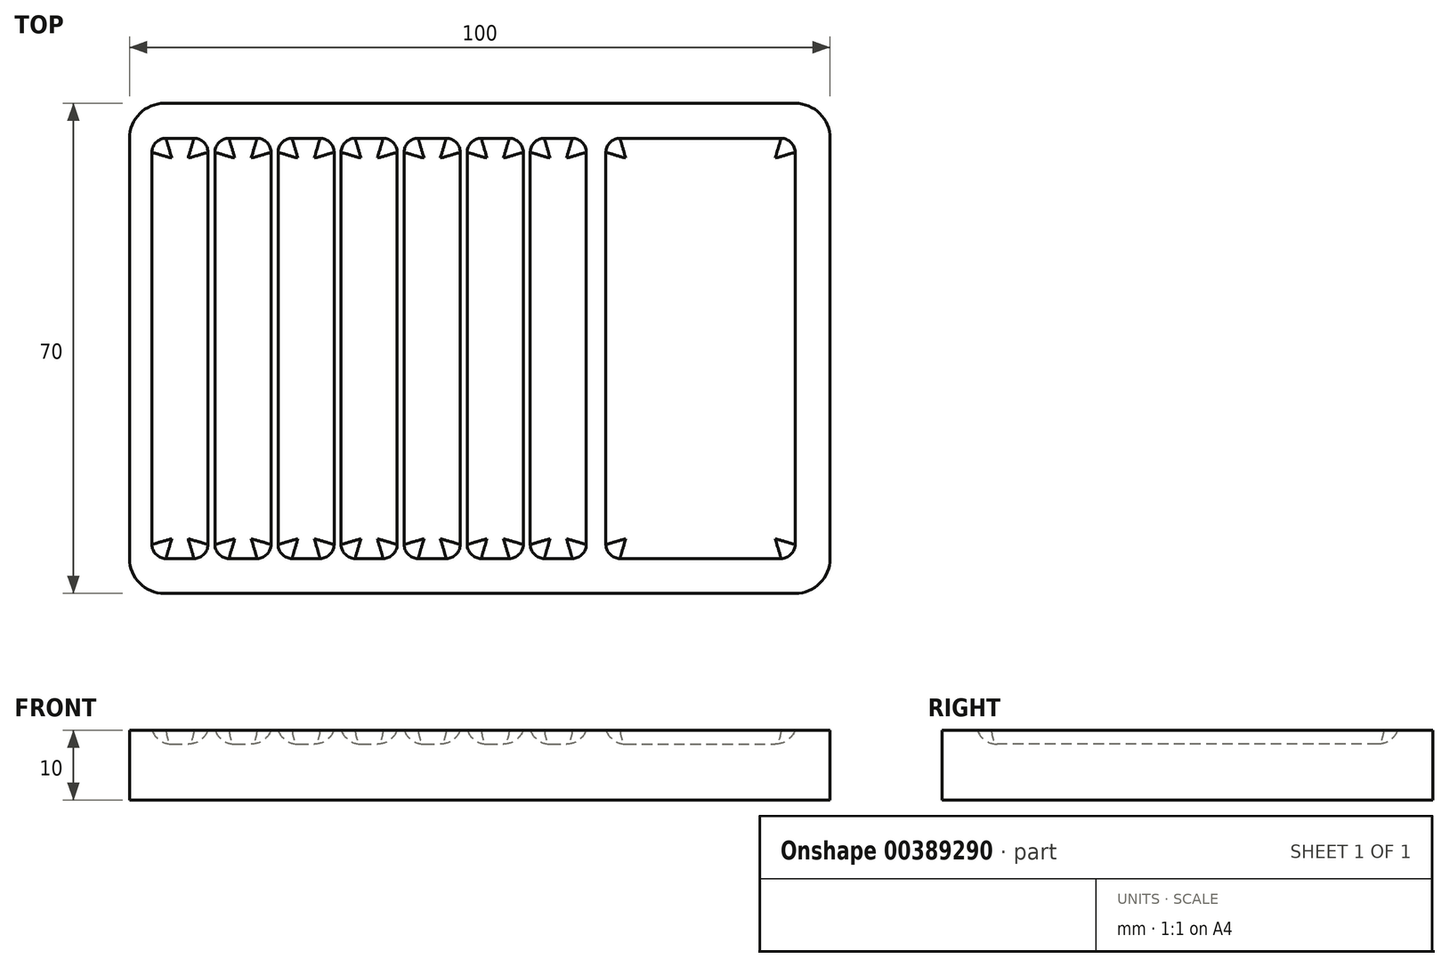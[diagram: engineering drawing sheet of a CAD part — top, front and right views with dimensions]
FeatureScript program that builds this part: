
annotation { "Feature Type Name" : "Feature", "Feature Type Description" : "" }
export const myFeature = defineFeature(function(context is Context, id is Id, definition is map)
    precondition{}
    {
        {
            var Q0;
            Q0=qCreatedBy(makeId("Top.planeOp"),FACE);
            var sketch = newSketch(context, id + "F0", { "sketchPlane" : qUnion([Q0])});
            skLineSegment(sketch, "E0.bottom", {"start": v(0, 0) * mm, "end": v(-100, 0) * mm});
            skLineSegment(sketch, "E0.top", {"start": v(0, 70) * mm, "end": v(-100, 70) * mm});
            skLineSegment(sketch, "E0.left", {"start": v(0, 0) * mm, "end": v(0, 70) * mm});
            skLineSegment(sketch, "E0.right", {"start": v(-100, 0) * mm, "end": v(-100, 70) * mm});
            skSolve(sketch);
        }
        {
            var Q0;
            Q0 = qSketchRegion(id + "F0", true);
            extrude(context, id + "F1", {"entities" : qUnion([Q0]), "depth" : 10 * mm, "offsetDistance" : 25 * mm});
        }
        {
            var Q0;
            Q0=makeQuery(id+"F1.opExtrude","CAP_FACE",FACE,{"disambiguationData":[OSD([sQuery(id+"F0.wireOp",EDGE,"E0.bottom"),sQuery(id+"F0.wireOp",EDGE,"E0.top"),sQuery(id+"F0.wireOp",EDGE,"E0.left"),sQuery(id+"F0.wireOp",EDGE,"E0.right")])],"isStart":false});
            var sketch = newSketch(context, id + "F2", { "sketchPlane" : qUnion([Q0])});
            skLineSegment(sketch, "E1.bottom", {"start": v(-94.8, 65) * mm, "end": v(-90.8, 65) * mm});
            skLineSegment(sketch, "E1.top", {"start": v(-94.8, 5) * mm, "end": v(-90.8, 5) * mm});
            skLineSegment(sketch, "E1.left", {"start": v(-96.8, 63) * mm, "end": v(-96.8, 7) * mm});
            skLineSegment(sketch, "E1.right", {"start": v(-88.8, 63) * mm, "end": v(-88.8, 7) * mm});
            skPoint(sketch, "E2.visualSharp", {"position": v(-88.8, 65) * mm});
            skArc(sketch, "E2.filletArc", {"start": v(-88.8, 63) * mm, "mid": v(-89.38, 64.41) * mm, "end": v(-90.8, 65) * mm});
            skPoint(sketch, "E3.visualSharp", {"position": v(-96.8, 65) * mm});
            skArc(sketch, "E3.filletArc", {"start": v(-94.8, 65) * mm, "mid": v(-96.2, 64.41) * mm, "end": v(-96.8, 63) * mm});
            skPoint(sketch, "E4.visualSharp", {"position": v(-88.8, 5) * mm});
            skArc(sketch, "E4.filletArc", {"start": v(-90.8, 5) * mm, "mid": v(-89.38, 5.59) * mm, "end": v(-88.8, 7) * mm});
            skPoint(sketch, "E5.visualSharp", {"position": v(-96.8, 5) * mm});
            skArc(sketch, "E5.filletArc", {"start": v(-96.8, 7) * mm, "mid": v(-96.2, 5.59) * mm, "end": v(-94.8, 5) * mm});
            skLineSegment(sketch, "E6.1.0.0", {"start": v(-79.8, 63) * mm, "end": v(-79.8, 7) * mm});
            skPoint(sketch, "E6.1.0.1", {"position": v(-79.8, 65) * mm});
            skLineSegment(sketch, "E6.1.0.2", {"start": v(-87.8, 63) * mm, "end": v(-87.8, 7) * mm});
            skPoint(sketch, "E6.1.0.3", {"position": v(-87.8, 65) * mm});
            skPoint(sketch, "E6.1.0.4", {"position": v(-87.8, 5) * mm});
            skPoint(sketch, "E6.1.0.5", {"position": v(-79.8, 5) * mm});
            skArc(sketch, "E6.1.0.6", {"start": v(-79.8, 63) * mm, "mid": v(-80.38, 64.41) * mm, "end": v(-81.8, 65) * mm});
            skArc(sketch, "E6.1.0.7", {"start": v(-81.8, 5) * mm, "mid": v(-80.38, 5.59) * mm, "end": v(-79.8, 7) * mm});
            skArc(sketch, "E6.1.0.8", {"start": v(-87.8, 7) * mm, "mid": v(-87.2, 5.59) * mm, "end": v(-85.8, 5) * mm});
            skArc(sketch, "E6.1.0.9", {"start": v(-85.8, 65) * mm, "mid": v(-87.2, 64.41) * mm, "end": v(-87.8, 63) * mm});
            skLineSegment(sketch, "E6.1.0.10", {"start": v(-85.8, 5) * mm, "end": v(-81.8, 5) * mm});
            skLineSegment(sketch, "E6.1.0.11", {"start": v(-85.8, 65) * mm, "end": v(-81.8, 65) * mm});
            skLineSegment(sketch, "E6.2.0.0", {"start": v(-70.8, 63) * mm, "end": v(-70.8, 7) * mm});
            skPoint(sketch, "E6.2.0.1", {"position": v(-70.8, 65) * mm});
            skLineSegment(sketch, "E6.2.0.2", {"start": v(-78.8, 63) * mm, "end": v(-78.8, 7) * mm});
            skPoint(sketch, "E6.2.0.3", {"position": v(-78.8, 65) * mm});
            skPoint(sketch, "E6.2.0.4", {"position": v(-78.8, 5) * mm});
            skPoint(sketch, "E6.2.0.5", {"position": v(-70.8, 5) * mm});
            skArc(sketch, "E6.2.0.6", {"start": v(-70.8, 63) * mm, "mid": v(-71.38, 64.41) * mm, "end": v(-72.8, 65) * mm});
            skArc(sketch, "E6.2.0.7", {"start": v(-72.8, 5) * mm, "mid": v(-71.38, 5.59) * mm, "end": v(-70.8, 7) * mm});
            skArc(sketch, "E6.2.0.8", {"start": v(-78.8, 7) * mm, "mid": v(-78.2, 5.59) * mm, "end": v(-76.8, 5) * mm});
            skArc(sketch, "E6.2.0.9", {"start": v(-76.8, 65) * mm, "mid": v(-78.2, 64.41) * mm, "end": v(-78.8, 63) * mm});
            skLineSegment(sketch, "E6.2.0.10", {"start": v(-76.8, 5) * mm, "end": v(-72.8, 5) * mm});
            skLineSegment(sketch, "E6.2.0.11", {"start": v(-76.8, 65) * mm, "end": v(-72.8, 65) * mm});
            skLineSegment(sketch, "E6.3.0.0", {"start": v(-61.8, 63) * mm, "end": v(-61.8, 7) * mm});
            skPoint(sketch, "E6.3.0.1", {"position": v(-61.8, 65) * mm});
            skLineSegment(sketch, "E6.3.0.2", {"start": v(-69.8, 63) * mm, "end": v(-69.8, 7) * mm});
            skPoint(sketch, "E6.3.0.3", {"position": v(-69.8, 65) * mm});
            skPoint(sketch, "E6.3.0.4", {"position": v(-69.8, 5) * mm});
            skPoint(sketch, "E6.3.0.5", {"position": v(-61.8, 5) * mm});
            skArc(sketch, "E6.3.0.6", {"start": v(-61.8, 63) * mm, "mid": v(-62.38, 64.41) * mm, "end": v(-63.8, 65) * mm});
            skArc(sketch, "E6.3.0.7", {"start": v(-63.8, 5) * mm, "mid": v(-62.38, 5.59) * mm, "end": v(-61.8, 7) * mm});
            skArc(sketch, "E6.3.0.8", {"start": v(-69.8, 7) * mm, "mid": v(-69.2, 5.59) * mm, "end": v(-67.8, 5) * mm});
            skArc(sketch, "E6.3.0.9", {"start": v(-67.8, 65) * mm, "mid": v(-69.2, 64.41) * mm, "end": v(-69.8, 63) * mm});
            skLineSegment(sketch, "E6.3.0.10", {"start": v(-67.8, 5) * mm, "end": v(-63.8, 5) * mm});
            skLineSegment(sketch, "E6.3.0.11", {"start": v(-67.8, 65) * mm, "end": v(-63.8, 65) * mm});
            skLineSegment(sketch, "E6.4.0.0", {"start": v(-52.8, 63) * mm, "end": v(-52.8, 7) * mm});
            skPoint(sketch, "E6.4.0.1", {"position": v(-52.8, 65) * mm});
            skLineSegment(sketch, "E6.4.0.2", {"start": v(-60.8, 63) * mm, "end": v(-60.8, 7) * mm});
            skPoint(sketch, "E6.4.0.3", {"position": v(-60.8, 65) * mm});
            skPoint(sketch, "E6.4.0.4", {"position": v(-60.8, 5) * mm});
            skPoint(sketch, "E6.4.0.5", {"position": v(-52.8, 5) * mm});
            skArc(sketch, "E6.4.0.6", {"start": v(-52.8, 63) * mm, "mid": v(-53.38, 64.41) * mm, "end": v(-54.8, 65) * mm});
            skArc(sketch, "E6.4.0.7", {"start": v(-54.8, 5) * mm, "mid": v(-53.38, 5.59) * mm, "end": v(-52.8, 7) * mm});
            skArc(sketch, "E6.4.0.8", {"start": v(-60.8, 7) * mm, "mid": v(-60.2, 5.59) * mm, "end": v(-58.8, 5) * mm});
            skArc(sketch, "E6.4.0.9", {"start": v(-58.8, 65) * mm, "mid": v(-60.2, 64.41) * mm, "end": v(-60.8, 63) * mm});
            skLineSegment(sketch, "E6.4.0.10", {"start": v(-58.8, 5) * mm, "end": v(-54.8, 5) * mm});
            skLineSegment(sketch, "E6.4.0.11", {"start": v(-58.8, 65) * mm, "end": v(-54.8, 65) * mm});
            skLineSegment(sketch, "E6.5.0.0", {"start": v(-43.8, 63) * mm, "end": v(-43.8, 7) * mm});
            skPoint(sketch, "E6.5.0.1", {"position": v(-43.8, 65) * mm});
            skLineSegment(sketch, "E6.5.0.2", {"start": v(-51.8, 63) * mm, "end": v(-51.8, 7) * mm});
            skPoint(sketch, "E6.5.0.3", {"position": v(-51.8, 65) * mm});
            skPoint(sketch, "E6.5.0.4", {"position": v(-51.8, 5) * mm});
            skPoint(sketch, "E6.5.0.5", {"position": v(-43.8, 5) * mm});
            skArc(sketch, "E6.5.0.6", {"start": v(-43.8, 63) * mm, "mid": v(-44.38, 64.41) * mm, "end": v(-45.8, 65) * mm});
            skArc(sketch, "E6.5.0.7", {"start": v(-45.8, 5) * mm, "mid": v(-44.38, 5.59) * mm, "end": v(-43.8, 7) * mm});
            skArc(sketch, "E6.5.0.8", {"start": v(-51.8, 7) * mm, "mid": v(-51.2, 5.59) * mm, "end": v(-49.8, 5) * mm});
            skArc(sketch, "E6.5.0.9", {"start": v(-49.8, 65) * mm, "mid": v(-51.2, 64.41) * mm, "end": v(-51.8, 63) * mm});
            skLineSegment(sketch, "E6.5.0.10", {"start": v(-49.8, 5) * mm, "end": v(-45.8, 5) * mm});
            skLineSegment(sketch, "E6.5.0.11", {"start": v(-49.8, 65) * mm, "end": v(-45.8, 65) * mm});
            skLineSegment(sketch, "E6.6.0.0", {"start": v(-34.8, 63) * mm, "end": v(-34.8, 7) * mm});
            skPoint(sketch, "E6.6.0.1", {"position": v(-34.8, 65) * mm});
            skLineSegment(sketch, "E6.6.0.2", {"start": v(-42.8, 63) * mm, "end": v(-42.8, 7) * mm});
            skPoint(sketch, "E6.6.0.3", {"position": v(-42.8, 65) * mm});
            skPoint(sketch, "E6.6.0.4", {"position": v(-42.8, 5) * mm});
            skPoint(sketch, "E6.6.0.5", {"position": v(-34.8, 5) * mm});
            skArc(sketch, "E6.6.0.6", {"start": v(-34.8, 63) * mm, "mid": v(-35.38, 64.41) * mm, "end": v(-36.8, 65) * mm});
            skArc(sketch, "E6.6.0.7", {"start": v(-36.8, 5) * mm, "mid": v(-35.38, 5.59) * mm, "end": v(-34.8, 7) * mm});
            skArc(sketch, "E6.6.0.8", {"start": v(-42.8, 7) * mm, "mid": v(-42.2, 5.59) * mm, "end": v(-40.8, 5) * mm});
            skArc(sketch, "E6.6.0.9", {"start": v(-40.8, 65) * mm, "mid": v(-42.2, 64.41) * mm, "end": v(-42.8, 63) * mm});
            skLineSegment(sketch, "E6.6.0.10", {"start": v(-40.8, 5) * mm, "end": v(-36.8, 5) * mm});
            skLineSegment(sketch, "E6.6.0.11", {"start": v(-40.8, 65) * mm, "end": v(-36.8, 65) * mm});
            skLineSegment(sketch, "E6.direction1", {"start": v(-96.8, 5) * mm, "end": v(-87.8, 5) * mm, "construction": true});
            skLineSegment(sketch, "E7.bottom", {"start": v(-30, 65) * mm, "end": v(-7, 65) * mm});
            skLineSegment(sketch, "E7.top", {"start": v(-30, 5) * mm, "end": v(-7, 5) * mm});
            skLineSegment(sketch, "E7.left", {"start": v(-32, 63) * mm, "end": v(-32, 7) * mm});
            skLineSegment(sketch, "E7.right", {"start": v(-5, 63) * mm, "end": v(-5, 7) * mm});
            skPoint(sketch, "E8.visualSharp", {"position": v(-32, 65) * mm});
            skArc(sketch, "E8.filletArc", {"start": v(-30, 65) * mm, "mid": v(-31.41, 64.41) * mm, "end": v(-32, 63) * mm});
            skPoint(sketch, "E9.visualSharp", {"position": v(-5, 65) * mm});
            skArc(sketch, "E9.filletArc", {"start": v(-5, 63) * mm, "mid": v(-5.59, 64.41) * mm, "end": v(-7, 65) * mm});
            skPoint(sketch, "E10.visualSharp", {"position": v(-5, 5) * mm});
            skArc(sketch, "E10.filletArc", {"start": v(-7, 5) * mm, "mid": v(-5.59, 5.59) * mm, "end": v(-5, 7) * mm});
            skPoint(sketch, "E11.visualSharp", {"position": v(-32, 5) * mm});
            skArc(sketch, "E11.filletArc", {"start": v(-32, 7) * mm, "mid": v(-31.41, 5.59) * mm, "end": v(-30, 5) * mm});
            skSolve(sketch);
        }
        {
            var Q0;
            Q0=makeQuery(id+"F2.imprint","IMPRINT",FACE,{"disambiguationData":[TD([[makeQuery(id+"F2.imprint","IMPRINT",EDGE,{"derivedFrom":sQuery(id+"F2.wireOp",EDGE,"E6.1.0.0")}),-1.0]])]});
            var Q1;
            Q1=makeQuery(id+"F2.imprint","IMPRINT",FACE,{"disambiguationData":[TD([[makeQuery(id+"F2.imprint","IMPRINT",EDGE,{"derivedFrom":sQuery(id+"F2.wireOp",EDGE,"E6.2.0.0")}),-1.0]])]});
            var Q2;
            Q2=makeQuery(id+"F2.imprint","IMPRINT",FACE,{"disambiguationData":[TD([[makeQuery(id+"F2.imprint","IMPRINT",EDGE,{"derivedFrom":sQuery(id+"F2.wireOp",EDGE,"E6.3.0.0")}),-1.0]])]});
            var Q3;
            Q3=makeQuery(id+"F2.imprint","IMPRINT",FACE,{"disambiguationData":[TD([[makeQuery(id+"F2.imprint","IMPRINT",EDGE,{"derivedFrom":sQuery(id+"F2.wireOp",EDGE,"E6.4.0.0")}),-1.0]])]});
            var Q4;
            Q4=makeQuery(id+"F2.imprint","IMPRINT",FACE,{"disambiguationData":[TD([[makeQuery(id+"F2.imprint","IMPRINT",EDGE,{"derivedFrom":sQuery(id+"F2.wireOp",EDGE,"E6.5.0.0")}),-1.0]])]});
            var Q5;
            Q5=makeQuery(id+"F2.imprint","IMPRINT",FACE,{"disambiguationData":[TD([[makeQuery(id+"F2.imprint","IMPRINT",EDGE,{"derivedFrom":sQuery(id+"F2.wireOp",EDGE,"E6.6.0.0")}),-1.0]])]});
            var Q6;
            Q6=makeQuery(id+"F2.imprint","IMPRINT",FACE,{"disambiguationData":[TD([[makeQuery(id+"F2.imprint","IMPRINT",EDGE,{"derivedFrom":sQuery(id+"F2.wireOp",EDGE,"E1.bottom")}),-1.0]])]});
            var Q7;
            Q7=makeQuery(id+"F2.imprint","IMPRINT",FACE,{"disambiguationData":[TD([[makeQuery(id+"F2.imprint","IMPRINT",EDGE,{"derivedFrom":sQuery(id+"F2.wireOp",EDGE,"E7.bottom")}),-1.0]])]});
            extrude(context, id + "F3", {"entities" : qUnion([Q0, Q1, Q2, Q3, Q4, Q5, Q6, Q7]), "operationType" : NewBodyOperationType.REMOVE, "oppositeDirection" : true, "depth" : 2 * mm, "offsetDistance" : 25 * mm});
        }
        {
            var Q0;
            Q0=makeQuery(id+"F3.boolean.opBoolean","COPY",FACE,{"derivedFrom":makeQuery(id+"F3.opExtrude","CAP_FACE",FACE,{"disambiguationData":[OSD([sQuery(id+"F2.wireOp",EDGE,"E1.bottom"),sQuery(id+"F2.wireOp",EDGE,"E1.top"),sQuery(id+"F2.wireOp",EDGE,"E1.left"),sQuery(id+"F2.wireOp",EDGE,"E1.right"),sQuery(id+"F2.wireOp",EDGE,"E2.filletArc"),sQuery(id+"F2.wireOp",EDGE,"E3.filletArc"),sQuery(id+"F2.wireOp",EDGE,"E4.filletArc"),sQuery(id+"F2.wireOp",EDGE,"E5.filletArc")])],"isStart":false})});
            var Q1;
            Q1=makeQuery(id+"F3.boolean.opBoolean","COPY",FACE,{"derivedFrom":makeQuery(id+"F3.opExtrude","CAP_FACE",FACE,{"disambiguationData":[OSD([sQuery(id+"F2.wireOp",EDGE,"E7.bottom"),sQuery(id+"F2.wireOp",EDGE,"E7.top"),sQuery(id+"F2.wireOp",EDGE,"E7.left"),sQuery(id+"F2.wireOp",EDGE,"E7.right"),sQuery(id+"F2.wireOp",EDGE,"E8.filletArc"),sQuery(id+"F2.wireOp",EDGE,"E9.filletArc"),sQuery(id+"F2.wireOp",EDGE,"E10.filletArc"),sQuery(id+"F2.wireOp",EDGE,"E11.filletArc")])],"isStart":false})});
            var Q2;
            Q2=makeQuery(id+"F3.boolean.opBoolean","COPY",FACE,{"derivedFrom":makeQuery(id+"F3.opExtrude","CAP_FACE",FACE,{"disambiguationData":[OSD([sQuery(id+"F2.wireOp",EDGE,"E6.1.0.0"),sQuery(id+"F2.wireOp",EDGE,"E6.1.0.2"),sQuery(id+"F2.wireOp",EDGE,"E6.1.0.6"),sQuery(id+"F2.wireOp",EDGE,"E6.1.0.7"),sQuery(id+"F2.wireOp",EDGE,"E6.1.0.8"),sQuery(id+"F2.wireOp",EDGE,"E6.1.0.9"),sQuery(id+"F2.wireOp",EDGE,"E6.1.0.10"),sQuery(id+"F2.wireOp",EDGE,"E6.1.0.11")])],"isStart":false})});
            var Q3;
            Q3=makeQuery(id+"F3.boolean.opBoolean","COPY",FACE,{"derivedFrom":makeQuery(id+"F3.opExtrude","CAP_FACE",FACE,{"disambiguationData":[OSD([sQuery(id+"F2.wireOp",EDGE,"E6.2.0.0"),sQuery(id+"F2.wireOp",EDGE,"E6.2.0.2"),sQuery(id+"F2.wireOp",EDGE,"E6.2.0.6"),sQuery(id+"F2.wireOp",EDGE,"E6.2.0.7"),sQuery(id+"F2.wireOp",EDGE,"E6.2.0.8"),sQuery(id+"F2.wireOp",EDGE,"E6.2.0.9"),sQuery(id+"F2.wireOp",EDGE,"E6.2.0.10"),sQuery(id+"F2.wireOp",EDGE,"E6.2.0.11")])],"isStart":false})});
            var Q4;
            Q4=makeQuery(id+"F3.boolean.opBoolean","COPY",FACE,{"derivedFrom":makeQuery(id+"F3.opExtrude","CAP_FACE",FACE,{"disambiguationData":[OSD([sQuery(id+"F2.wireOp",EDGE,"E6.3.0.0"),sQuery(id+"F2.wireOp",EDGE,"E6.3.0.2"),sQuery(id+"F2.wireOp",EDGE,"E6.3.0.6"),sQuery(id+"F2.wireOp",EDGE,"E6.3.0.7"),sQuery(id+"F2.wireOp",EDGE,"E6.3.0.8"),sQuery(id+"F2.wireOp",EDGE,"E6.3.0.9"),sQuery(id+"F2.wireOp",EDGE,"E6.3.0.10"),sQuery(id+"F2.wireOp",EDGE,"E6.3.0.11")])],"isStart":false})});
            var Q5;
            Q5=makeQuery(id+"F3.boolean.opBoolean","COPY",FACE,{"derivedFrom":makeQuery(id+"F3.opExtrude","CAP_FACE",FACE,{"disambiguationData":[OSD([sQuery(id+"F2.wireOp",EDGE,"E6.4.0.0"),sQuery(id+"F2.wireOp",EDGE,"E6.4.0.2"),sQuery(id+"F2.wireOp",EDGE,"E6.4.0.6"),sQuery(id+"F2.wireOp",EDGE,"E6.4.0.7"),sQuery(id+"F2.wireOp",EDGE,"E6.4.0.8"),sQuery(id+"F2.wireOp",EDGE,"E6.4.0.9"),sQuery(id+"F2.wireOp",EDGE,"E6.4.0.10"),sQuery(id+"F2.wireOp",EDGE,"E6.4.0.11")])],"isStart":false})});
            var Q6;
            Q6=makeQuery(id+"F3.boolean.opBoolean","COPY",FACE,{"derivedFrom":makeQuery(id+"F3.opExtrude","CAP_FACE",FACE,{"disambiguationData":[OSD([sQuery(id+"F2.wireOp",EDGE,"E6.5.0.0"),sQuery(id+"F2.wireOp",EDGE,"E6.5.0.2"),sQuery(id+"F2.wireOp",EDGE,"E6.5.0.6"),sQuery(id+"F2.wireOp",EDGE,"E6.5.0.7"),sQuery(id+"F2.wireOp",EDGE,"E6.5.0.8"),sQuery(id+"F2.wireOp",EDGE,"E6.5.0.9"),sQuery(id+"F2.wireOp",EDGE,"E6.5.0.10"),sQuery(id+"F2.wireOp",EDGE,"E6.5.0.11")])],"isStart":false})});
            var Q7;
            Q7=makeQuery(id+"F3.boolean.opBoolean","COPY",FACE,{"derivedFrom":makeQuery(id+"F3.opExtrude","CAP_FACE",FACE,{"disambiguationData":[OSD([sQuery(id+"F2.wireOp",EDGE,"E6.6.0.0"),sQuery(id+"F2.wireOp",EDGE,"E6.6.0.2"),sQuery(id+"F2.wireOp",EDGE,"E6.6.0.6"),sQuery(id+"F2.wireOp",EDGE,"E6.6.0.7"),sQuery(id+"F2.wireOp",EDGE,"E6.6.0.8"),sQuery(id+"F2.wireOp",EDGE,"E6.6.0.9"),sQuery(id+"F2.wireOp",EDGE,"E6.6.0.10"),sQuery(id+"F2.wireOp",EDGE,"E6.6.0.11")])],"isStart":false})});
            fillet(context, id + "F4", {"entities" : qUnion([Q0, Q1, Q2, Q3, Q4, Q5, Q6, Q7]), "radius" : 3 * mm, "tangentPropagation" : true, "allowEdgeOverflow" : false});
        }
        {
            var Q0;
            Q0=makeQuery(id+"F1.opExtrude","SWEPT_EDGE",EDGE,{"disambiguationData":[OSD([sQuery(id+"F0.wireOp",EDGE,"E0.top"),sQuery(id+"F0.wireOp",EDGE,"E0.left")])]});
            var Q1;
            Q1=makeQuery(id+"F1.opExtrude","SWEPT_EDGE",EDGE,{"disambiguationData":[OSD([sQuery(id+"F0.wireOp",EDGE,"E0.bottom"),sQuery(id+"F0.wireOp",EDGE,"E0.left")])]});
            var Q2;
            Q2=makeQuery(id+"F1.opExtrude","SWEPT_EDGE",EDGE,{"disambiguationData":[OSD([sQuery(id+"F0.wireOp",EDGE,"E0.bottom"),sQuery(id+"F0.wireOp",EDGE,"E0.right")])]});
            var Q3;
            Q3=makeQuery(id+"F1.opExtrude","SWEPT_EDGE",EDGE,{"disambiguationData":[OSD([sQuery(id+"F0.wireOp",EDGE,"E0.top"),sQuery(id+"F0.wireOp",EDGE,"E0.right")])]});
            fillet(context, id + "F5", {"entities" : qUnion([Q0, Q1, Q2, Q3]), "radius" : 5 * mm, "tangentPropagation" : true, "allowEdgeOverflow" : false});
        }
    });
